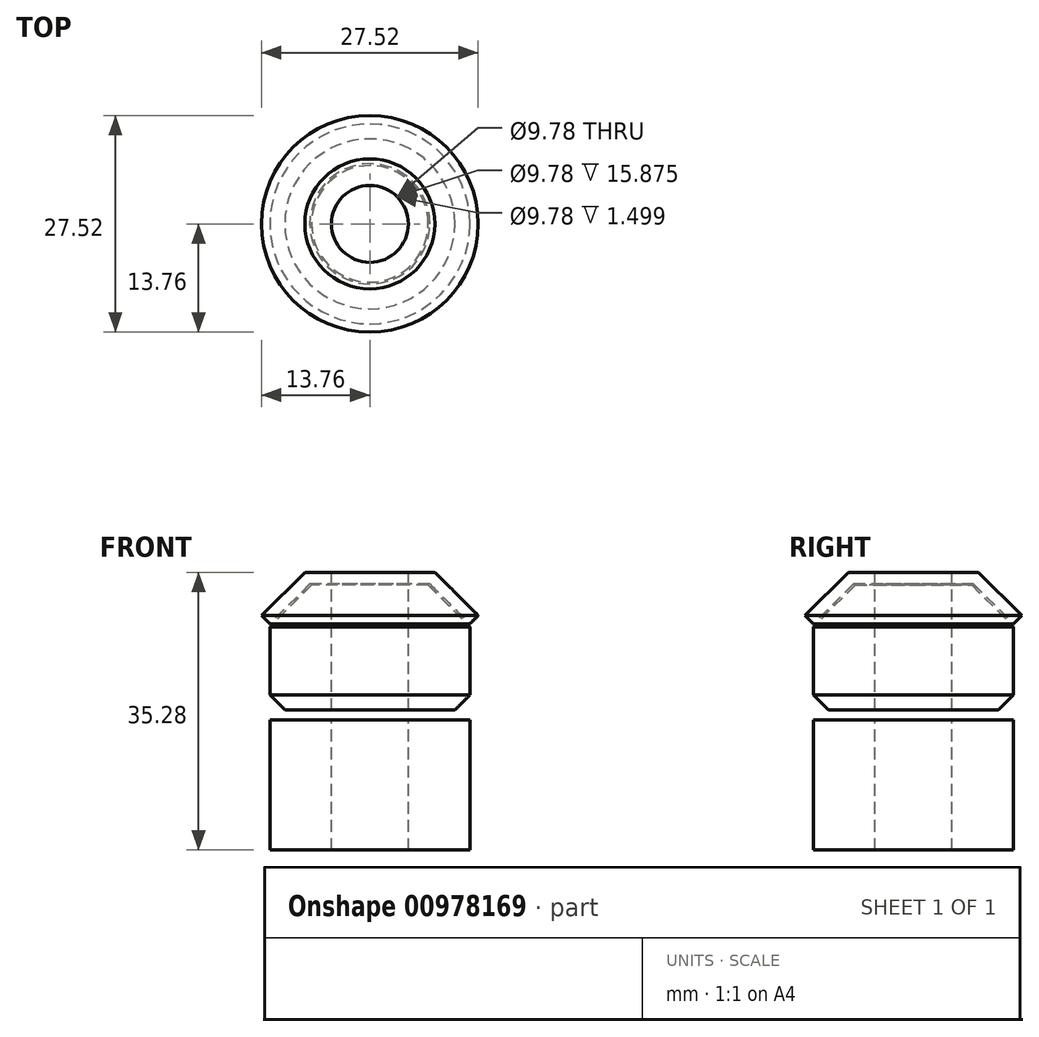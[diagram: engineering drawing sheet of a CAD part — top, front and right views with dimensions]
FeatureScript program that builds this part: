
annotation { "Feature Type Name" : "Feature", "Feature Type Description" : "" }
export const myFeature = defineFeature(function(context is Context, id is Id, definition is map)
    precondition{}
    {
        {
            var Q0;
            Q0=qCreatedBy(makeId("Front.planeOp"),FACE);
            var sketch = newSketch(context, id + "F0", { "sketchPlane" : qUnion([Q0])});
            skLineSegment(sketch, "E0", {"start": v(12.7, 25.45) * mm, "end": v(12.7, 16) * mm, "construction": true});
            skLineSegment(sketch, "E1", {"start": v(0, 43) * mm, "end": v(0, -55) * mm, "construction": true});
            skLineSegment(sketch, "E2.bottom", {"start": v(12.7, -17.78) * mm, "end": v(4.89, -17.78) * mm});
            skLineSegment(sketch, "E2.top", {"start": v(12.7, -1.27) * mm, "end": v(4.89, -1.27) * mm});
            skLineSegment(sketch, "E2.left", {"start": v(12.7, -17.78) * mm, "end": v(12.7, -1.27) * mm});
            skLineSegment(sketch, "E2.right", {"start": v(4.89, -17.78) * mm, "end": v(4.89, -1.27) * mm});
            skLineSegment(sketch, "E3", {"start": v(10.8, 0) * mm, "end": v(4.89, 0) * mm});
            skLineSegment(sketch, "E4", {"start": v(4.89, 0) * mm, "end": v(4.89, 15.87) * mm});
            skLineSegment(sketch, "E5", {"start": v(4.89, 15.87) * mm, "end": v(7.4, 15.87) * mm});
            skLineSegment(sketch, "E6", {"start": v(7.4, 15.87) * mm, "end": v(12.7, 10.58) * mm});
            skLineSegment(sketch, "E7", {"start": v(12.7, 10.58) * mm, "end": v(12.7, 1.9) * mm});
            skLineSegment(sketch, "E8", {"start": v(12.7, 10.94) * mm, "end": v(7.64, 16) * mm});
            skLineSegment(sketch, "E9", {"start": v(7.64, 16) * mm, "end": v(4.89, 16) * mm});
            skLineSegment(sketch, "E10", {"start": v(4.89, 16) * mm, "end": v(4.89, 17.5) * mm});
            skLineSegment(sketch, "E11", {"start": v(4.89, 17.5) * mm, "end": v(8.26, 17.5) * mm});
            skLineSegment(sketch, "E12", {"start": v(10.8, 0) * mm, "end": v(12.7, 1.9) * mm});
            skLineSegment(sketch, "E13.trimOffspring", {"start": v(12.7, 0) * mm, "end": v(12.7, -32.75) * mm, "construction": true});
            skLineSegment(sketch, "E14.trimOffspring", {"start": v(12.7, 10.94) * mm, "end": v(12.7, 1.9) * mm, "construction": true});
            skLineSegment(sketch, "E15", {"start": v(12.7, 10.94) * mm, "end": v(13.76, 12) * mm});
            skLineSegment(sketch, "E16", {"start": v(13.76, 12) * mm, "end": v(8.26, 17.5) * mm});
            skSolve(sketch);
        }
        {
            var Q0;
            Q0 = qSketchRegion(id + "F0", true);
            var Q1;
            Q1=sQuery(id+"F0.wireOp",EDGE,"E1");
            revolve(context, id + "F1", {"surfaceOperationType" : NewSurfaceOperationType.NEW, "entities" : qUnion([Q0]), "axis" : qUnion([Q1]), "revolveType" : RevolveType.FULL});
        }
    });
